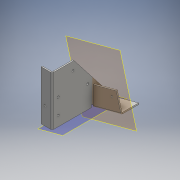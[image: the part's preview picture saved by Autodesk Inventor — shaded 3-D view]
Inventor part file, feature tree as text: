
AUTODESK INVENTOR PART (.ipt)
format: ipt  version: 2016 (Build 200138000, 138)  size: 284,672 bytes
history: native  units: mm
features: sheet_metal_op x7, hole x6, sketch x5, other x5, plane x2
ambient origin geometry x8: Origin, YZ Plane, XZ Plane, XY Plane, X Axis, Y Axis, Z Axis, Center Point
bodies: Body1 (feature_tree)
feature tree (25):
  sheet_metal_op  "Face10"
  sheet_metal_op  "Face11"
  plane  "Work Plane8"
  sheet_metal_op  "Face12"
  plane  "Work Plane9"
  sheet_metal_op  "Face13"
  hole  "Hole14"  [1 undecoded]
  hole  "Hole15"  [1 undecoded]
  hole  "Hole16"  [1 undecoded]
  hole  "Hole17"  [1 undecoded]
  hole  "Hole18"  [1 undecoded]
  hole  "Hole19"  [1 undecoded]
  sketch  "Sketch13"  dims[d13=3.0mm d209=125.0mm]
  other  "Plate10"
  sketch  "Sketch14"  dims[d211=55.0mm d212=90.0deg]
  other  "Plate11"
  sheet_metal_op  "Bend9"
  sketch  "Sketch15"  dims[d213=22.340214mm d218=101.6mm]
  other  "Plate12"
  sheet_metal_op  "Bend10"
  sketch  "Sketch16"  dims[d219=45.0mm d220=0.0mm]
  other  "Plate13"
  sheet_metal_op  "Bend11"
  sketch  "Sketch17"  dims[d221=3.0mm d222=25.0mm d223=0.0mm d224=125.0mm d225=90.0deg d226=1.5mm d227=3.0mm d228=1.5mm d229=6.0mm d230=3.0mm d231=15.0deg d232=75.0mm d233=90.0deg d234=45.0mm d235=90.0deg d236=1.5mm d237=3.0mm d238=1.5mm d239=6.0mm d240=3.0mm d241=45.0mm d242=90.0deg d243=90.0deg d244=0.5mm d245=3.0mm d246=1.5mm d247=6.0mm d248=3.0mm d249=15.0mm d250=15.0mm d251=5.0mm d252=6.0mm d253=4.0mm d254=2.0mm d255=90.0deg d256=3.0mm d257=20.594885mm d258=15.0mm d259=50.0mm d260=5.0mm d261=6.0mm d262=4.0mm d263=2.0mm d264=90.0deg d265=3.0mm d266=20.594885mm d267=5.0mm d268=5.0mm d269=15.0mm d270=9.075712mm d271=6.632251mm d272=15.0mm d273=60.0mm d274=5.0mm d275=6.0mm d276=4.0mm d277=2.0mm d278=90.0deg d279=3.0mm d280=20.594885mm d281=15.0mm d282=60.0mm d283=5.0mm d284=6.0mm d285=4.0mm d286=2.0mm d287=90.0deg d288=3.0mm d289=20.594885mm d290=15.0mm d291=100.0mm d292=5.0mm d293=6.0mm d294=4.0mm d295=2.0mm d296=90.0deg d297=3.0mm d298=20.594885mm d299=10.0mm d300=45.0mm d301=5.0mm d302=6.0mm d303=4.0mm d304=2.0mm d305=90.0deg d306=3.0mm d307=20.594885mm]
  other  "Definition1"
note: 6 required parameter values undecoded (feature->parameter linkage not recoverable at this tier; creation-order binding heuristic only, values carry confidence <= 0.55)
